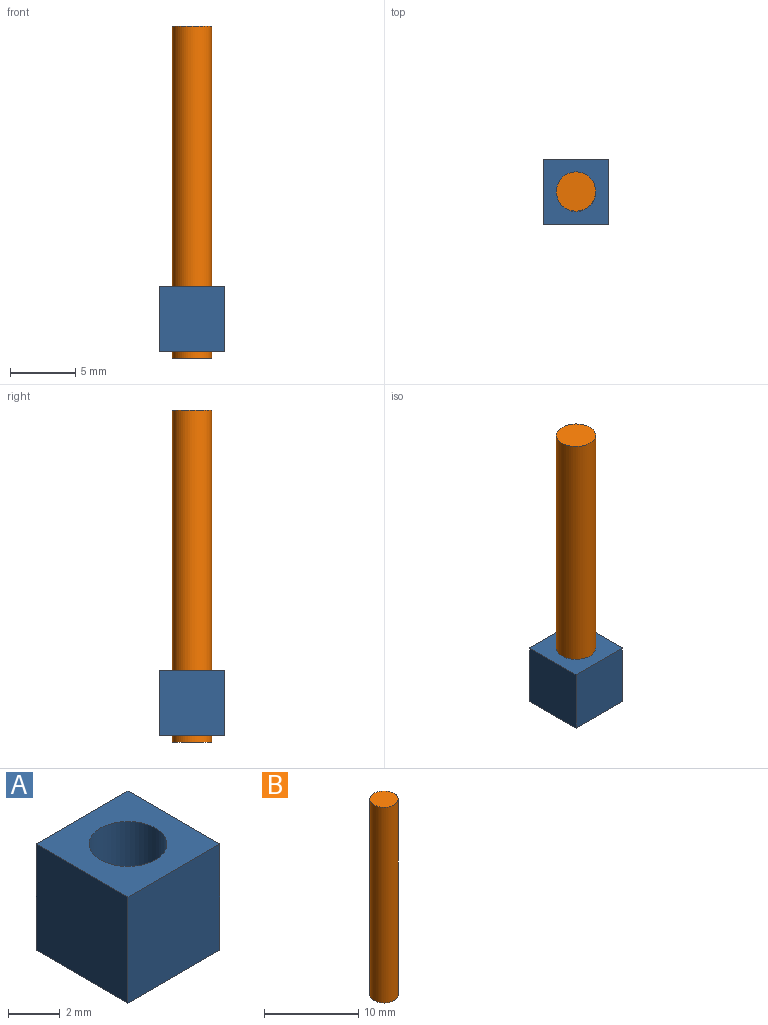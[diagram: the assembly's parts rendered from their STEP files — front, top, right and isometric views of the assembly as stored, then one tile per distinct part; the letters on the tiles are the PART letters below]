
ASSEMBLY  parts=2 mates=1
PART A: 7 faces, bbox 5x5x5 mm
  f0: plane 5x5mm, normal (-1,0,0), area 25mm2, adj f1,f4,f5,f6
  f1: plane 5x5mm, normal (0,-1,0), area 25mm2, adj f0,f2,f5,f6
  f2: plane 5x5mm, normal (1,0,0), area 25mm2, adj f1,f4,f5,f6
  f3: cylinder r=1.5mm len=5mm, axis (0,0,-1), area 47.1mm2, adj f5,f6
  f4: plane 5x5mm, normal (0,1,0), area 25mm2, adj f0,f2,f5,f6
  f5: plane 5x5mm, normal (0,0,1), area 17.9mm2, adj f0,f1,f2,f3,f4
  f6: plane 5x5mm, normal (0,0,-1), area 17.9mm2, adj f0,f1,f2,f3,f4
PART B: 3 faces, bbox 3x3x25.4 mm
  f0: cylinder r=1.5mm len=25.4mm, axis (0,0,-1), area 239.4mm2, adj f1,f2
  f1: plane 3x3mm, normal (0,0,1), area 7.1mm2, adj f0
  f2: plane 3x3mm, normal (0,0,-1), area 7.1mm2, adj f0
PLACE A t=(0.87,1.14,0)mm fixed
PLACE B rot(axis=(0,0,1),19deg) t=(0.87,1.14,-0.47)mm
MATE cylindrical B.f0 <-> A.f3  axis (0,0,-1) through (0.87,1.14,12.23)mm
